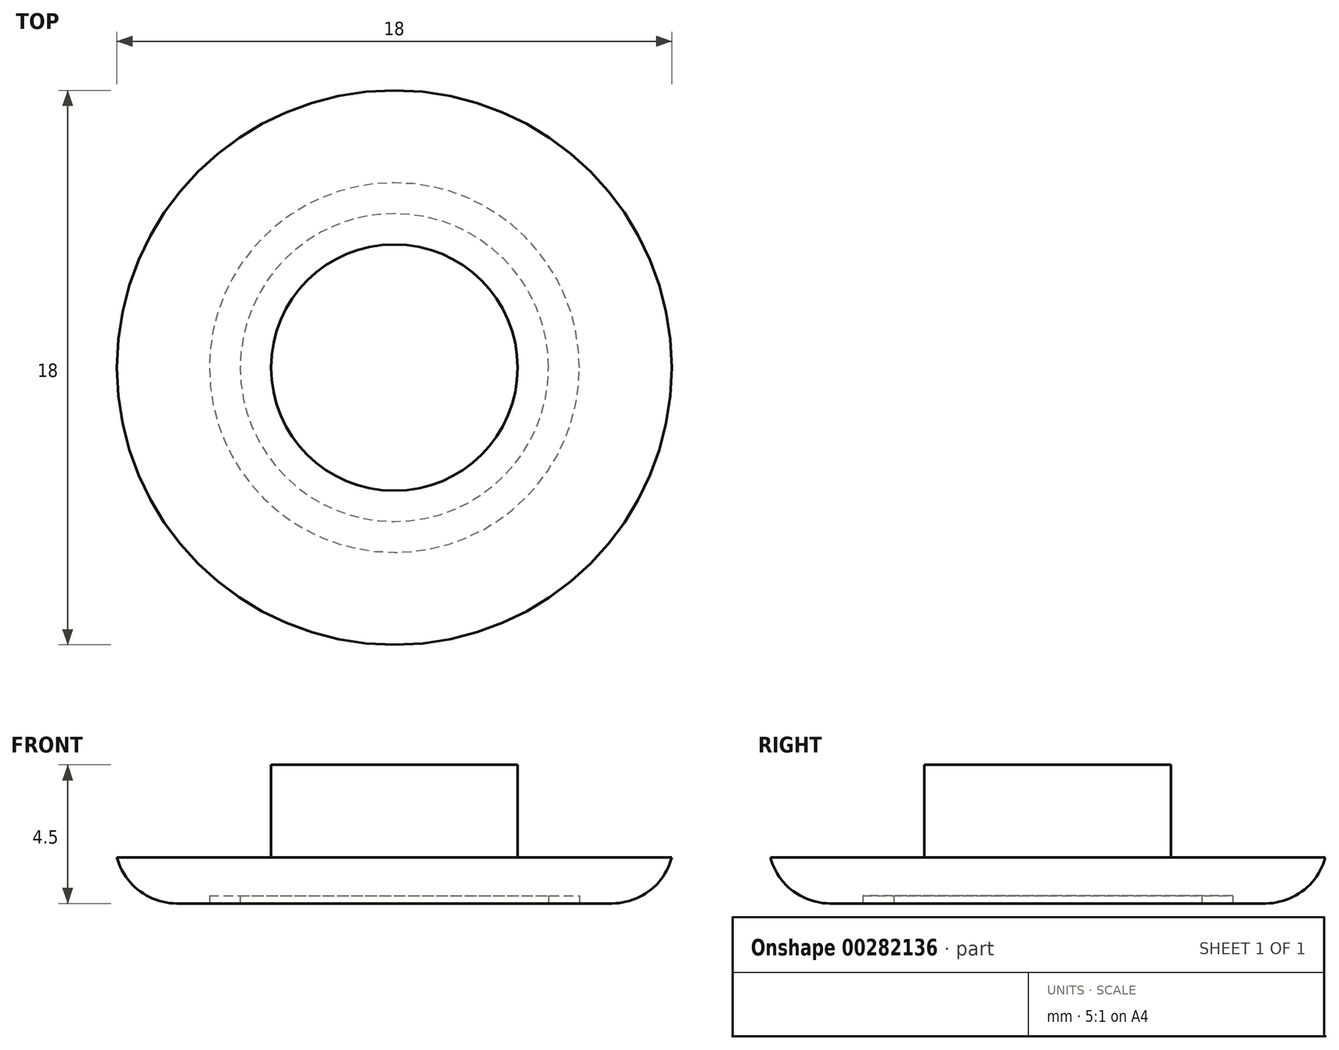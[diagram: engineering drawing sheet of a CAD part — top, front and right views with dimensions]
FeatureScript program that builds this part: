
annotation { "Feature Type Name" : "Feature", "Feature Type Description" : "" }
export const myFeature = defineFeature(function(context is Context, id is Id, definition is map)
    precondition{}
    {
        {
            var Q0;
            Q0=qCreatedBy(makeId("Top.planeOp"),FACE);
            var sketch = newSketch(context, id + "F0", { "sketchPlane" : qUnion([Q0])});
            skCircle(sketch, "E0", {"center": v(0, 0) * mm, "radius": 9 * mm});
            skSolve(sketch);
        }
        {
            var Q0;
            Q0=qSketchRegion(id+"F0",true);
            extrude(context, id + "F1", {"entities" : qUnion([Q0]), "depth" : 1.5 * mm, "offsetDistance" : 25 * mm});
        }
        {
            var Q0;
            Q0=makeQuery(id+"F1.opExtrude","CAP_FACE",FACE,{"disambiguationData":[OSD([sQuery(id+"F0.wireOp",EDGE,"E0")])],"isStart":false});
            var sketch = newSketch(context, id + "F2", { "sketchPlane" : qUnion([Q0])});
            skCircle(sketch, "E1", {"center": v(0, 0) * mm, "radius": 4 * mm});
            skSolve(sketch);
        }
        {
            var Q0;
            Q0=qSketchRegion(id+"F2",true);
            extrude(context, id + "F3", {"entities" : qUnion([Q0]), "operationType" : NewBodyOperationType.ADD, "depth" : 3 * mm});
        }
        {
            var Q0;
            Q0=makeQuery(id+"F1.opExtrude","CAP_EDGE",EDGE,{"disambiguationData":[OSD([sQuery(id+"F0.wireOp",EDGE,"E0")])],"isStart":true});
            fillet(context, id + "F4", {"entities" : qUnion([Q0]), "radius" : 2 * mm, "tangentPropagation" : true, "allowEdgeOverflow" : false});
        }
        {
            var Q0;
            Q0=makeQuery(id+"F1.opExtrude","CAP_FACE",FACE,{"disambiguationData":[OSD([sQuery(id+"F0.wireOp",EDGE,"E0")])],"isStart":true});
            var sketch = newSketch(context, id + "F5", { "sketchPlane" : qUnion([Q0])});
            skCircle(sketch, "E2.cCircle", {"center": v(0, 0) * mm, "radius": 7.06 * mm, "construction": true});
            skCircle(sketch, "E3", {"center": v(0, 0) * mm, "radius": 6 * mm});
            skCircle(sketch, "E4", {"center": v(0, 0) * mm, "radius": 5 * mm});
            skLineSegment(sketch, "E5", {"start": v(0, 0) * mm, "end": v(5, 0) * mm});
            skLineSegment(sketch, "E6", {"start": v(0, 0) * mm, "end": v(0, 5) * mm});
            skLineSegment(sketch, "E7", {"start": v(0, 0) * mm, "end": v(-5, 0) * mm});
            skLineSegment(sketch, "E8", {"start": v(0, 0) * mm, "end": v(0, -5) * mm});
            skLineSegment(sketch, "E9", {"start": v(0, 5) * mm, "end": v(-5, 0) * mm});
            skLineSegment(sketch, "E10", {"start": v(0, 5) * mm, "end": v(5, 0) * mm});
            skLineSegment(sketch, "E11", {"start": v(5, 0) * mm, "end": v(0, -5) * mm});
            skLineSegment(sketch, "E12", {"start": v(-5, 0) * mm, "end": v(0, -5) * mm});
            skLineSegment(sketch, "E13", {"start": v(-2.5, 2.5) * mm, "end": v(2.5, -2.5) * mm});
            skLineSegment(sketch, "E14", {"start": v(2.5, 2.5) * mm, "end": v(-2.5, -2.5) * mm});
            skSolve(sketch);
        }
        {
            var Q0;
            Q0=makeQuery(id+"F5.imprint","IMPRINT",FACE,{"disambiguationData":[TD([[makeQuery(id+"F5.imprint","IMPRINT",EDGE,{"derivedFrom":sQuery(id+"F5.wireOp",EDGE,"E3")}),1.0]])]});
            extrude(context, id + "F6", {"entities" : qUnion([Q0]), "operationType" : NewBodyOperationType.REMOVE, "oppositeDirection" : true, "depth" : .25 * mm, "offsetDistance" : 25 * mm});
        }
    });
